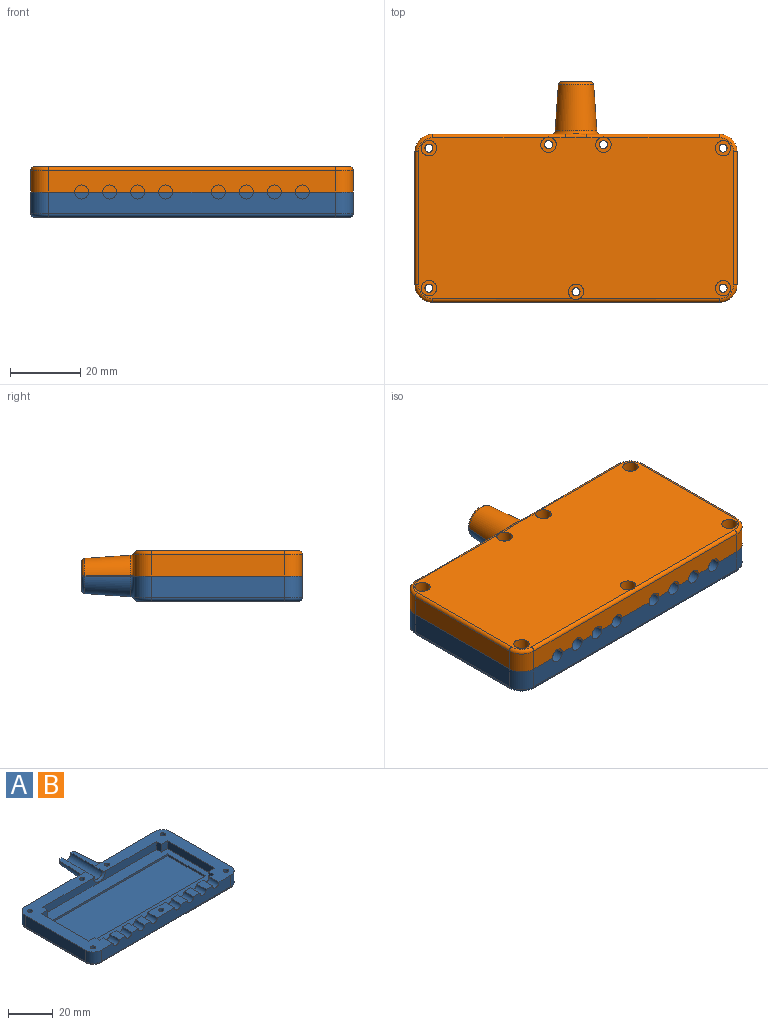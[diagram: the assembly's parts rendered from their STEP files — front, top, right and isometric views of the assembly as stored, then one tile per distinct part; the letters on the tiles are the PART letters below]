
ASSEMBLY  parts=2 mates=1
PART A: 84 faces, bbox 92.9x63.4x8 mm
  f0: plane 90x46.14mm, normal (0,0,-1), area 4021mm2, adj f60,f61,f62,f63,f64,f65,f66,f67
  f1: cylinder r=1.15mm len=4.2mm, axis (0,0,1), area 30.3mm2, adj f20,f82
  f2: cylinder r=1.15mm len=4.2mm, axis (0,0,1), area 30.3mm2, adj f20,f80
  f3: cylinder r=1.15mm len=4.2mm, axis (0,0,1), area 30.3mm2, adj f20,f74
  f4: cylinder r=1.15mm len=4.2mm, axis (0,0,1), area 30.3mm2, adj f16,f79
  f5: cylinder r=1.15mm len=4.2mm, axis (0,0,1), area 30.3mm2, adj f16,f77
  f6: cylinder r=1.15mm len=4.2mm, axis (0,0,1), area 30.3mm2, adj f16,f73
  f7: cylinder r=1.15mm len=4.2mm, axis (0,0,1), area 30.3mm2, adj f19,f70
  f8: plane 37.9x6.21mm, normal (0,1,0), area 218mm2, adj f16,f34,f36,f65
  f9: plane 80x36mm, normal (0,0,1), area 1069.4mm2, adj f10,f11,f12,f13,f39,f40,f41,f42
  f10: plane 72x4.3mm, normal (0,-1,0), area 286.3mm2, adj f9,f16,f20,f38,f57,f59
  f11: plane 72x4.3mm, normal (0,1,0), area 259.3mm2, adj f9,f15,f16,f17,f18,f19,f20,f21
  f12: plane 30x4.3mm, normal (-1,0,0), area 129mm2, adj f9,f16,f54,f58
  f13: plane 30x4.3mm, normal (1,0,0), area 129mm2, adj f9,f20,f52,f56
  f14: plane 82x6.2mm, normal (0,-1,0), area 458.1mm2, adj f15,f16,f17,f18,f19,f20,f21,f22
  f15: plane 6x4mm, normal (0,0,1), area 24mm2, adj f11,f14,f50,f51
  f16: plane 48x43.15mm, normal (0,0,1), area 550.5mm2, adj f4,f5,f6,f8,f10,f11,f12,f14
  f17: plane 6x4mm, normal (0,0,1), area 24mm2, adj f11,f14,f49,f50
  f18: plane 6x4mm, normal (0,0,1), area 24mm2, adj f11,f14,f48,f49
  f19: plane 11x6mm, normal (0,0,1), area 61.8mm2, adj f7,f11,f14,f44,f48
  f20: plane 48x43.15mm, normal (0,0,1), area 550.5mm2, adj f1,f2,f3,f10,f11,f13,f14,f24
  f21: plane 6x4mm, normal (0,0,1), area 24mm2, adj f11,f14,f46,f47
  f22: plane 6x4mm, normal (0,0,1), area 24mm2, adj f11,f14,f45,f46
  f23: plane 6x4mm, normal (0,0,1), area 24mm2, adj f11,f14,f44,f45
  f24: plane 15.03x4.12mm, normal (0,0,1), area 39.7mm2, adj f20,f28,f29,f35,f36,f37
  f25: plane 37.9x6.21mm, normal (0,1,0), area 218mm2, adj f20,f31,f36,f61
  f26: plane 38x6.2mm, normal (-1,0,0), area 235.6mm2, adj f20,f31,f32,f62
  f27: plane 38x6.2mm, normal (1,0,0), area 235.6mm2, adj f16,f33,f34,f69
  f28: plane 8.13x4.03mm, normal (0,1,0), area 12.9mm2, adj f24,f30,f35,f37
  f29: bspline ~15x12mm, area 226.9mm2, adj f24,f30,f35,f36
  f30: plane 15.03x4.12mm, normal (0,0,1), area 39.7mm2, adj f16,f28,f29,f35,f36,f37
  f31: cylinder r=5mm len=6.2mm, axis (0,0,1), area 48.7mm2, adj f20,f25,f26,f60
  f32: cylinder r=5mm len=6.2mm, axis (0,0,-1), area 48.7mm2, adj f14,f20,f26,f64
  f33: cylinder r=5mm len=6.2mm, axis (0,0,1), area 48.7mm2, adj f14,f16,f27,f68
  f34: cylinder r=5mm len=6.2mm, axis (0,0,-1), area 48.7mm2, adj f8,f16,f27,f67
  f35: bspline ~10.13x5.82mm, area 22mm2, adj f24,f28,f29,f30
  f36: bspline ~13.87x7.43mm, area 29.8mm2, adj f8,f24,f25,f29,f30,f63
  f37: cylinder r=2.85mm len=20mm, axis (0,1,0), area 179.3mm2, adj f16,f20,f24,f28,f30,f38
  f38: torus R=3.85mm, axis (0,1,0), area 15.9mm2, adj f10,f16,f20,f37
  f39: plane 24x1mm, normal (1,0,0), area 24mm2, adj f9,f40,f42,f43
  f40: plane 73.44x1mm, normal (0,-1,0), area 73.4mm2, adj f9,f39,f41,f43
  f41: plane 24x1mm, normal (-1,0,0), area 24mm2, adj f9,f40,f42,f43
  f42: plane 73.44x1mm, normal (0,1,0), area 73.4mm2, adj f9,f39,f41,f43
  f43: plane 73.44x24mm, normal (0,0,1), area 1762.6mm2, adj f39,f40,f41,f42
  f44: cylinder r=2mm len=6mm, axis (0,-1,0), area 37.7mm2, adj f11,f14,f19,f23
  f45: cylinder r=2mm len=6mm, axis (0,-1,0), area 37.7mm2, adj f11,f14,f22,f23
  f46: cylinder r=2mm len=6mm, axis (0,-1,0), area 37.7mm2, adj f11,f14,f21,f22
  f47: cylinder r=2mm len=6mm, axis (0,-1,0), area 37.7mm2, adj f11,f14,f20,f21
  f48: cylinder r=2mm len=6mm, axis (0,-1,0), area 37.7mm2, adj f11,f14,f18,f19
  f49: cylinder r=2mm len=6mm, axis (0,-1,0), area 37.7mm2, adj f11,f14,f17,f18
  f50: cylinder r=2mm len=6mm, axis (0,-1,0), area 37.7mm2, adj f11,f14,f15,f17
  f51: cylinder r=2mm len=6mm, axis (0,-1,0), area 37.7mm2, adj f11,f14,f15,f16
  f52: plane 4.3x4mm, normal (0,1,0), area 17.2mm2, adj f9,f13,f20,f53
  f53: plane 4.3x3mm, normal (1,0,0), area 12.9mm2, adj f9,f11,f20,f52
  f54: plane 4.3x4mm, normal (0,1,0), area 17.2mm2, adj f9,f12,f16,f55
  f55: plane 4.3x3mm, normal (-1,0,0), area 12.9mm2, adj f9,f11,f16,f54
  f56: plane 4.3x4mm, normal (0,-1,0), area 17.2mm2, adj f9,f13,f20,f57
  f57: plane 4.3x3mm, normal (1,0,0), area 12.9mm2, adj f9,f10,f20,f56
  f58: plane 4.3x4mm, normal (0,-1,0), area 17.2mm2, adj f9,f12,f16,f59
  f59: plane 4.3x3mm, normal (-1,0,0), area 12.9mm2, adj f9,f10,f16,f58
  f60: torus R=4mm, axis (0,0,1), area 11.4mm2, adj f0,f31,f61,f62
  f61: cylinder r=1mm len=37.9mm, axis (-1,0,0), area 59.3mm2, adj f0,f25,f60,f63,f75
  f62: cylinder r=1mm len=38mm, axis (0,-1,0), area 59.7mm2, adj f0,f26,f60,f64
  f63: bspline ~7.33x1.17mm, area 8.2mm2, adj f0,f36,f61,f65
  f64: torus R=4mm, axis (0,0,1), area 11.4mm2, adj f0,f32,f62,f66
  f65: cylinder r=1mm len=37.9mm, axis (-1,0,0), area 59.3mm2, adj f0,f8,f63,f67,f72
  f66: cylinder r=1mm len=82mm, axis (1,0,0), area 128.6mm2, adj f0,f14,f64,f68,f71
  f67: torus R=4mm, axis (0,0,1), area 11.4mm2, adj f0,f34,f65,f69
  f68: torus R=4mm, axis (0,0,1), area 11.4mm2, adj f0,f33,f66,f69
  f69: cylinder r=1mm len=38mm, axis (0,1,0), area 59.7mm2, adj f0,f27,f67,f68
  f70: plane 4.4x4.4mm, normal (0,0,-1), area 11.1mm2, adj f7,f71
  f71: cylinder r=2.2mm len=4.4mm, axis (0,0,-1), area 41.5mm2, adj f0,f66,f70
  f72: cylinder r=2.2mm len=4.4mm, axis (0,0,-1), area 41.5mm2, adj f0,f65,f73
  f73: plane 4.4x4.4mm, normal (0,0,-1), area 11.1mm2, adj f6,f72
  f74: plane 4.4x4.4mm, normal (0,0,-1), area 11.1mm2, adj f3,f75
  f75: cylinder r=2.2mm len=4.4mm, axis (0,0,-1), area 41.5mm2, adj f0,f61,f74
  f76: cylinder r=2.2mm len=4.4mm, axis (0,0,-1), area 41.5mm2, adj f0,f77
  f77: plane 4.4x4.4mm, normal (0,0,-1), area 11.1mm2, adj f5,f76
  f78: cylinder r=2.2mm len=4.4mm, axis (0,0,-1), area 41.5mm2, adj f0,f79
  f79: plane 4.4x4.4mm, normal (0,0,-1), area 11.1mm2, adj f4,f78
  f80: plane 4.4x4.4mm, normal (0,0,-1), area 11.1mm2, adj f2,f81
  f81: cylinder r=2.2mm len=4.4mm, axis (0,0,-1), area 41.5mm2, adj f0,f80
  f82: plane 4.4x4.4mm, normal (0,0,-1), area 11.1mm2, adj f1,f83
  f83: cylinder r=2.2mm len=4.4mm, axis (0,0,-1), area 41.5mm2, adj f0,f82
PART B: same geometry as A
PLACE A t=(-20.69,-22.64,-6.35)mm
PLACE B rot(axis=(0,1,0),180deg) t=(-20.69,-22.64,8.05)mm
MATE fastened B.f4 <-> A.f1  axis (0,0,-1) through (-62.69,-42.64,0.85)mm
